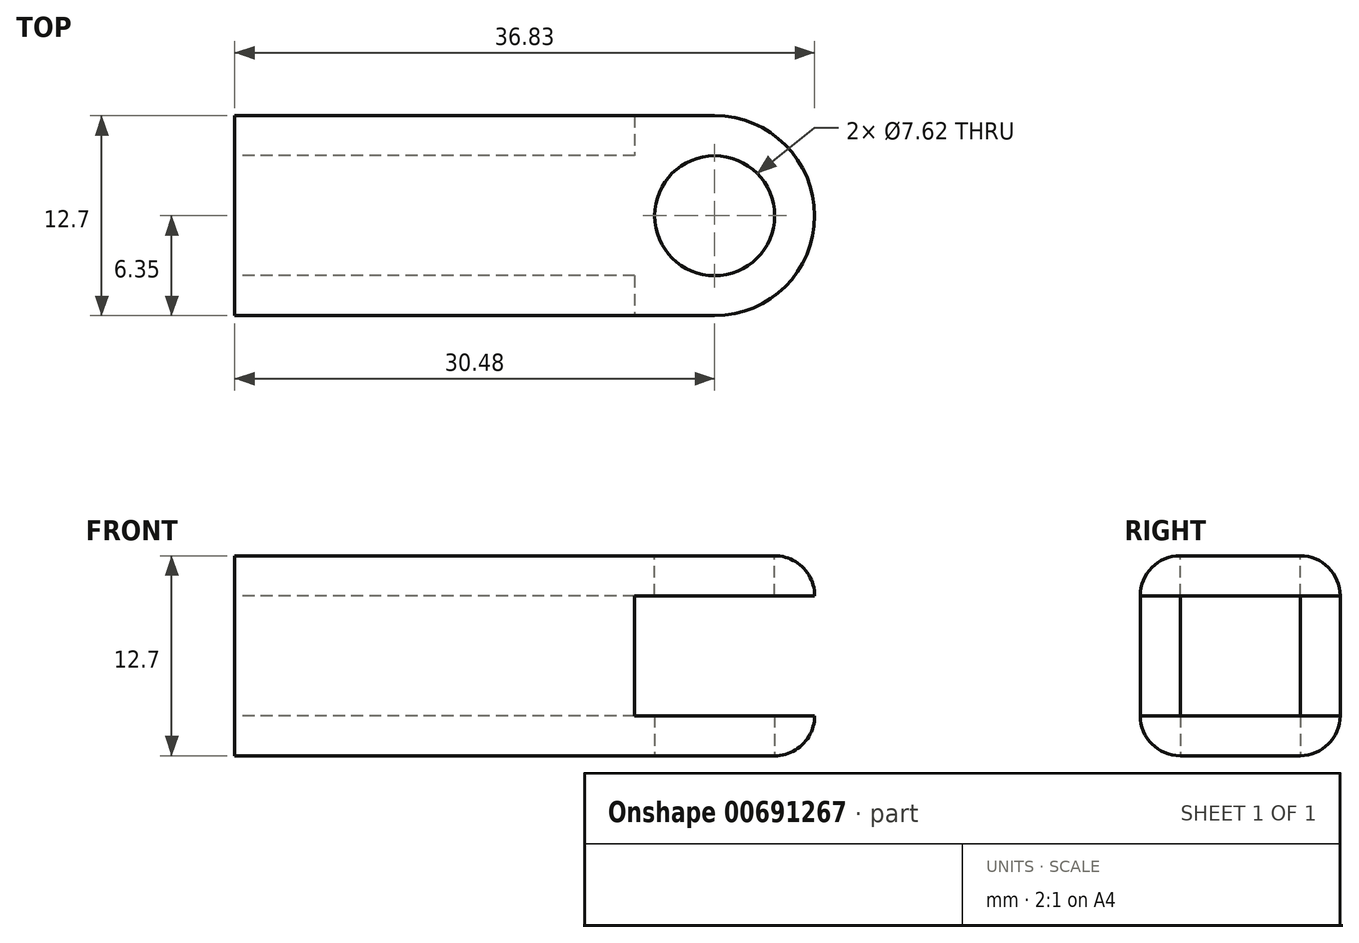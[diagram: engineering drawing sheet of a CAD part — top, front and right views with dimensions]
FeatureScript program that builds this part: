
annotation { "Feature Type Name" : "Feature", "Feature Type Description" : "" }
export const myFeature = defineFeature(function(context is Context, id is Id, definition is map)
    precondition{}
    {
        {
            var Q0;
            Q0=qCreatedBy(makeId("Right.planeOp"),FACE);
            var sketch = newSketch(context, id + "F0", { "sketchPlane" : qUnion([Q0])});
            skLineSegment(sketch, "E0.bottom", {"start": v(0, 0) * mm, "end": v(-12.7, 0) * mm});
            skLineSegment(sketch, "E0.top", {"start": v(0, -12.7) * mm, "end": v(-12.7, -12.7) * mm});
            skLineSegment(sketch, "E0.left", {"start": v(0, 0) * mm, "end": v(0, -12.7) * mm});
            skLineSegment(sketch, "E0.right", {"start": v(-12.7, 0) * mm, "end": v(-12.7, -12.7) * mm});
            skLineSegment(sketch, "E1", {"start": v(0, -6.35) * mm, "end": v(-2.54, -6.35) * mm});
            skLineSegment(sketch, "E2", {"start": v(-2.54, -6.35) * mm, "end": v(-2.54, -10.16) * mm});
            skLineSegment(sketch, "E3", {"start": v(-2.54, -6.35) * mm, "end": v(-2.54, -2.54) * mm});
            skLineSegment(sketch, "E4", {"start": v(-2.54, -10.16) * mm, "end": v(-10.16, -10.16) * mm});
            skLineSegment(sketch, "E5", {"start": v(-10.16, -10.16) * mm, "end": v(-10.16, -2.54) * mm});
            skLineSegment(sketch, "E6", {"start": v(-10.16, -2.54) * mm, "end": v(-2.54, -2.54) * mm});
            skSolve(sketch);
        }
        {
            var Q0;
            {var subQ3=sQuery(id+"F0.wireOp",EDGE,"E0.bottom");Q0=makeQuery(id+"F0.imprint","IMPRINT",FACE,{"disambiguationData":[TD([[makeQuery(id+"F0.imprint","IMPRINT",EDGE,{"derivedFrom":subQ3}),1.0]])]});}
            extrude(context, id + "F1", {"entities" : qUnion([Q0]), "depth" : 25.4 * mm, "offsetDistance" : 25.4 * mm});
        }
        {
            var Q0;
            Q0=makeQuery(id+"F1.opExtrude","SWEPT_FACE",FACE,{"disambiguationData":[OSD([sQuery(id+"F0.wireOp",EDGE,"E0.bottom")])]});
            var sketch = newSketch(context, id + "F2", { "sketchPlane" : qUnion([Q0])});
            skLineSegment(sketch, "E7", {"start": v(25.4, 0) * mm, "end": v(30.48, 0) * mm});
            skLineSegment(sketch, "E8", {"start": v(25.4, -12.7) * mm, "end": v(30.48, -12.7) * mm});
            skArc(sketch, "E9", {"start": v(25.4, -10.16) * mm, "mid": v(36.83, -6.35) * mm, "end": v(25.4, -2.54) * mm});
            skCircle(sketch, "E10", {"center": v(30.48, -6.35) * mm, "radius": 3.81 * mm});
            skLineSegment(sketch, "E11", {"start": v(25.4, 0) * mm, "end": v(25.4, -12.7) * mm});
            skSolve(sketch);
        }
        {
            var Q0;
            {var subQ0=sQuery(id+"F2.wireOp",EDGE,"E7");Q0=makeQuery(id+"F2.imprint","IMPRINT",FACE,{"disambiguationData":[TD([[makeQuery(id+"F2.imprint","IMPRINT",EDGE,{"derivedFrom":subQ0}),-1.0]])]});}
            var Q1;
            Q1=makeQuery(id+"F2.imprint","IMPRINT",FACE,{"disambiguationData":[TD([[makeQuery(id+"F2.imprint","IMPRINT",EDGE,{"derivedFrom":sQuery(id+"F2.wireOp",EDGE,"E10")}),-1.0]])]});
            var Q2;
            {var subQ0=sQuery(id+"F2.wireOp",EDGE,"E8");Q2=makeQuery(id+"F2.imprint","IMPRINT",FACE,{"disambiguationData":[TD([[makeQuery(id+"F2.imprint","IMPRINT",EDGE,{"derivedFrom":subQ0}),1.0]])]});}
            extrude(context, id + "F3", {"entities" : qUnion([Q0, Q1, Q2]), "operationType" : NewBodyOperationType.ADD, "oppositeDirection" : true, "depth" : 2.54 * mm, "offsetDistance" : 25.4 * mm});
        }
        {
            var Q0;
            Q0=makeQuery(id+"F1.opExtrude","SWEPT_FACE",FACE,{"disambiguationData":[OSD([sQuery(id+"F0.wireOp",EDGE,"E0.top")])]});
            var sketch = newSketch(context, id + "F4", { "sketchPlane" : qUnion([Q0])});
            skLineSegment(sketch, "E12", {"start": v(25.4, 0) * mm, "end": v(30.48, 0) * mm});
            skLineSegment(sketch, "E13", {"start": v(25.4, 12.7) * mm, "end": v(30.48, 12.7) * mm});
            skLineSegment(sketch, "E14", {"start": v(30.48, 0) * mm, "end": v(30.48, 12.7) * mm});
            skArc(sketch, "E15", {"start": v(25.4, 2.54) * mm, "mid": v(36.83, 6.35) * mm, "end": v(25.4, 10.16) * mm});
            skCircle(sketch, "E16", {"center": v(30.48, 6.35) * mm, "radius": 3.81 * mm});
            skLineSegment(sketch, "E17", {"start": v(25.4, 12.7) * mm, "end": v(25.4, 0) * mm});
            skSolve(sketch);
        }
        {
            var Q0;
            {var subQ1=sQuery(id+"F4.wireOp",EDGE,"E14");var subQ6=sQuery(id+"F4.wireOp",EDGE,"E16");var subQ9=makeQuery(id+"F4.imprint","INTERSECT",VERTEX,{"disambiguationData":[OD(0.0)],"derivedFrom":[subQ1,subQ6]});Q0=makeQuery(id+"F4.imprint","IMPRINT",FACE,{"disambiguationData":[TD([[makeQuery(id+"F4.imprint","IMPRINT",EDGE,{"disambiguationData":[TD([[subQ9,1.0]])],"derivedFrom":subQ6}),-1.0]])]});}
            var Q1;
            {var subQ1=sQuery(id+"F4.wireOp",EDGE,"E14");var subQ3=sQuery(id+"F4.wireOp",EDGE,"E16");var subQ4=makeQuery(id+"F4.imprint","INTERSECT",VERTEX,{"disambiguationData":[OD(0.0)],"derivedFrom":[subQ1,subQ3]});Q1=makeQuery(id+"F4.imprint","IMPRINT",FACE,{"disambiguationData":[TD([[makeQuery(id+"F4.imprint","IMPRINT",EDGE,{"disambiguationData":[TD([[subQ4,-1.0]])],"derivedFrom":subQ3}),-1.0]])]});}
            var Q2;
            {var subQ0=sQuery(id+"F4.wireOp",EDGE,"E12");Q2=makeQuery(id+"F4.imprint","IMPRINT",FACE,{"disambiguationData":[TD([[makeQuery(id+"F4.imprint","IMPRINT",EDGE,{"derivedFrom":subQ0}),1.0]])]});}
            var Q3;
            {var subQ0=sQuery(id+"F4.wireOp",EDGE,"E13");Q3=makeQuery(id+"F4.imprint","IMPRINT",FACE,{"disambiguationData":[TD([[makeQuery(id+"F4.imprint","IMPRINT",EDGE,{"derivedFrom":subQ0}),-1.0]])]});}
            extrude(context, id + "F5", {"entities" : qUnion([Q0, Q1, Q2, Q3]), "operationType" : NewBodyOperationType.ADD, "oppositeDirection" : true, "depth" : 2.54 * mm, "offsetDistance" : 25.4 * mm});
        }
        {
            var Q0;
            Q0=makeQuery(id+"F3.boolean.opBoolean","MERGE",EDGE,{"derivedFrom":[makeQuery(id+"F1.opExtrude","SWEPT_EDGE",EDGE,{"disambiguationData":[OSD([sQuery(id+"F0.wireOp",EDGE,"E0.bottom"),sQuery(id+"F0.wireOp",EDGE,"E0.left")])]}),makeQuery(id+"F3.opExtrude","CAP_EDGE",EDGE,{"disambiguationData":[OSD([sQuery(id+"F2.wireOp",EDGE,"E7")])],"isStart":true})]});
            var Q1;
            Q1=makeQuery(id+"F3.opExtrude","CAP_EDGE",EDGE,{"disambiguationData":[OSD([sQuery(id+"F2.wireOp",EDGE,"E9")])],"isStart":true});
            var Q2;
            Q2=makeQuery(id+"F3.boolean.opBoolean","MERGE",EDGE,{"derivedFrom":[makeQuery(id+"F1.opExtrude","SWEPT_EDGE",EDGE,{"disambiguationData":[OSD([sQuery(id+"F0.wireOp",EDGE,"E0.bottom"),sQuery(id+"F0.wireOp",EDGE,"E0.right")])]}),makeQuery(id+"F3.opExtrude","CAP_EDGE",EDGE,{"disambiguationData":[OSD([sQuery(id+"F2.wireOp",EDGE,"E8")])],"isStart":true})]});
            fillet(context, id + "F6", {"entities" : qUnion([Q0, Q1, Q2]), "radius" : 2.54 * mm, "tangentPropagation" : true, "allowEdgeOverflow" : false});
        }
        {
            var Q0;
            Q0=makeQuery(id+"F5.boolean.opBoolean","MERGE",EDGE,{"derivedFrom":[makeQuery(id+"F1.opExtrude","SWEPT_EDGE",EDGE,{"disambiguationData":[OSD([sQuery(id+"F0.wireOp",EDGE,"E0.top"),sQuery(id+"F0.wireOp",EDGE,"E0.left")])]}),makeQuery(id+"F5.opExtrude","CAP_EDGE",EDGE,{"disambiguationData":[OSD([sQuery(id+"F4.wireOp",EDGE,"E12")])],"isStart":true})]});
            var Q1;
            Q1=makeQuery(id+"F5.opExtrude","CAP_EDGE",EDGE,{"disambiguationData":[OSD([sQuery(id+"F4.wireOp",EDGE,"E15")])],"isStart":true});
            var Q2;
            Q2=makeQuery(id+"F5.boolean.opBoolean","MERGE",EDGE,{"derivedFrom":[makeQuery(id+"F1.opExtrude","SWEPT_EDGE",EDGE,{"disambiguationData":[OSD([sQuery(id+"F0.wireOp",EDGE,"E0.top"),sQuery(id+"F0.wireOp",EDGE,"E0.right")])]}),makeQuery(id+"F5.opExtrude","CAP_EDGE",EDGE,{"disambiguationData":[OSD([sQuery(id+"F4.wireOp",EDGE,"E13")])],"isStart":true})]});
            fillet(context, id + "F7", {"entities" : qUnion([Q0, Q1, Q2]), "radius" : 2.54 * mm, "tangentPropagation" : true, "allowEdgeOverflow" : false});
        }
    });
